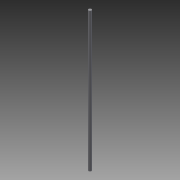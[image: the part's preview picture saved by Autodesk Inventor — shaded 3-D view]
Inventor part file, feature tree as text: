
AUTODESK INVENTOR PART (.ipt)
format: ipt  version: 2013 (Build 170138000, 138)  size: 68,096 bytes
history: native  units: in
note: dims shown in document units (in); Inventor stores cm internally (conversion verified against a paired STEP export)
features: other x2, extrude x1, sketch x1
ambient origin geometry x8: Origin, YZ Plane, XZ Plane, XY Plane, X Axis, Y Axis, Z Axis, Center Point
bodies: Solid1 (feature_tree)
feature tree (4):
  other  "Table"
  other  "almRod.5-01"
  extrude  "Extrusion1"  TaperAngle=0.0deg  [1 undecoded]
  sketch  "Sketch1"  dims[d0=0.5in d2=0.0in]
note: 1 required parameter value undecoded (feature->parameter linkage not recoverable at this tier; creation-order binding heuristic only, values carry confidence <= 0.55)
